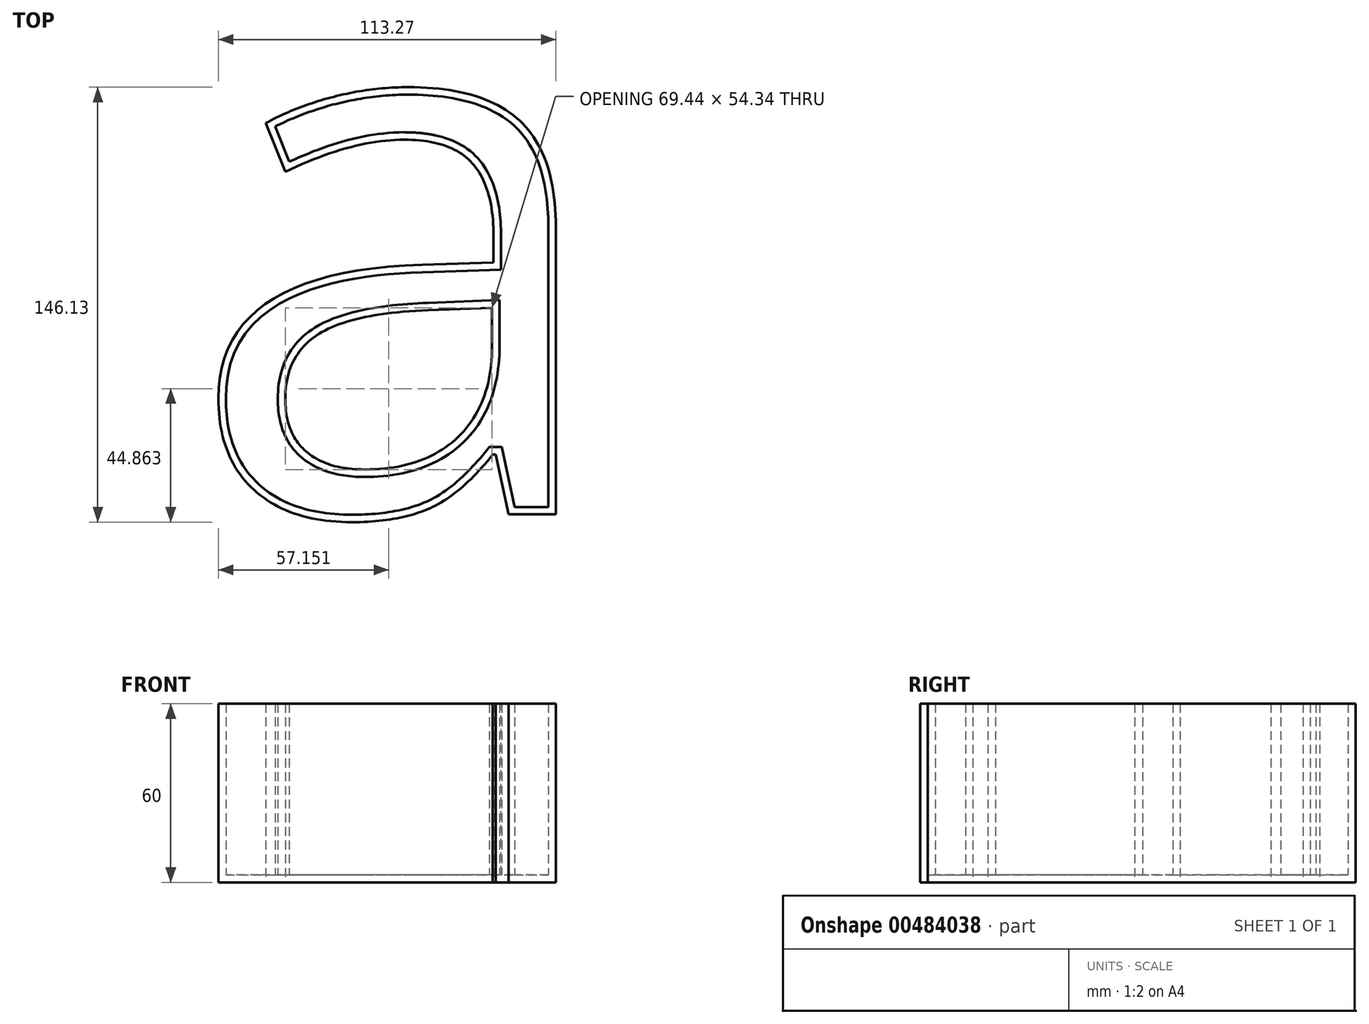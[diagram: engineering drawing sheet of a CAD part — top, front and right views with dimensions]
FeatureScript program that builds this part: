
annotation { "Feature Type Name" : "Feature", "Feature Type Description" : "" }
export const myFeature = defineFeature(function(context is Context, id is Id, definition is map)
    precondition{}
    {
        {
            var Q0;
            Q0=qCreatedBy(makeId("Top.planeOp"),FACE);
            var sketch = newSketch(context, id + "F0", { "sketchPlane" : qUnion([Q0])});
            skText(sketch, "E0", { "text": "a", "fontName": "OpenSans-Regular.ttf"});
            const initialGuessF0  = {"E0": [-0.07238, -0.06656, 1, 0, 0.19]};
            skSetInitialGuess(sketch, initialGuessF0);
            skSolve(sketch);
        }
        {
            var Q0;
            Q0 = qSketchRegion(id + "F0", true);
            extrude(context, id + "F1", {"entities" : qUnion([Q0]), "depth" : 60 * mm});
        }
        {
            var Q0;
            Q0=makeQuery(id+"F1.opExtrude","CAP_FACE",FACE,{"disambiguationData":[OSD([sQuery(id+"F0.wireOp",EDGE,"E0.sketch_text.stroke-0"),sQuery(id+"F0.wireOp",EDGE,"E0.sketch_text.stroke-1"),sQuery(id+"F0.wireOp",EDGE,"E0.sketch_text.stroke-2"),sQuery(id+"F0.wireOp",EDGE,"E0.sketch_text.stroke-3"),sQuery(id+"F0.wireOp",EDGE,"E0.sketch_text.stroke-4"),sQuery(id+"F0.wireOp",EDGE,"E0.sketch_text.stroke-5"),sQuery(id+"F0.wireOp",EDGE,"E0.sketch_text.stroke-6"),sQuery(id+"F0.wireOp",EDGE,"E0.sketch_text.stroke-7"),sQuery(id+"F0.wireOp",EDGE,"E0.sketch_text.stroke-8"),sQuery(id+"F0.wireOp",EDGE,"E0.sketch_text.stroke-9"),sQuery(id+"F0.wireOp",EDGE,"E0.sketch_text.stroke-10"),sQuery(id+"F0.wireOp",EDGE,"E0.sketch_text.stroke-11"),sQuery(id+"F0.wireOp",EDGE,"E0.sketch_text.stroke-12"),sQuery(id+"F0.wireOp",EDGE,"E0.sketch_text.stroke-13"),sQuery(id+"F0.wireOp",EDGE,"E0.sketch_text.stroke-14"),sQuery(id+"F0.wireOp",EDGE,"E0.sketch_text.stroke-15"),sQuery(id+"F0.wireOp",EDGE,"E0.sketch_text.stroke-16"),sQuery(id+"F0.wireOp",EDGE,"E0.sketch_text.stroke-17"),sQuery(id+"F0.wireOp",EDGE,"E0.sketch_text.stroke-18"),sQuery(id+"F0.wireOp",EDGE,"E0.sketch_text.stroke-19"),sQuery(id+"F0.wireOp",EDGE,"E0.sketch_text.stroke-20"),sQuery(id+"F0.wireOp",EDGE,"E0.sketch_text.stroke-21"),sQuery(id+"F0.wireOp",EDGE,"E0.sketch_text.stroke-22"),sQuery(id+"F0.wireOp",EDGE,"E0.sketch_text.stroke-23"),sQuery(id+"F0.wireOp",EDGE,"E0.sketch_text.stroke-24"),sQuery(id+"F0.wireOp",EDGE,"E0.sketch_text.stroke-25"),sQuery(id+"F0.wireOp",EDGE,"E0.sketch_text.stroke-26")])],"isStart":false});
            shell(context, id + "F2", {"entities" : qUnion([Q0]), "thickness" : 2.5 * mm});
        }
    });
